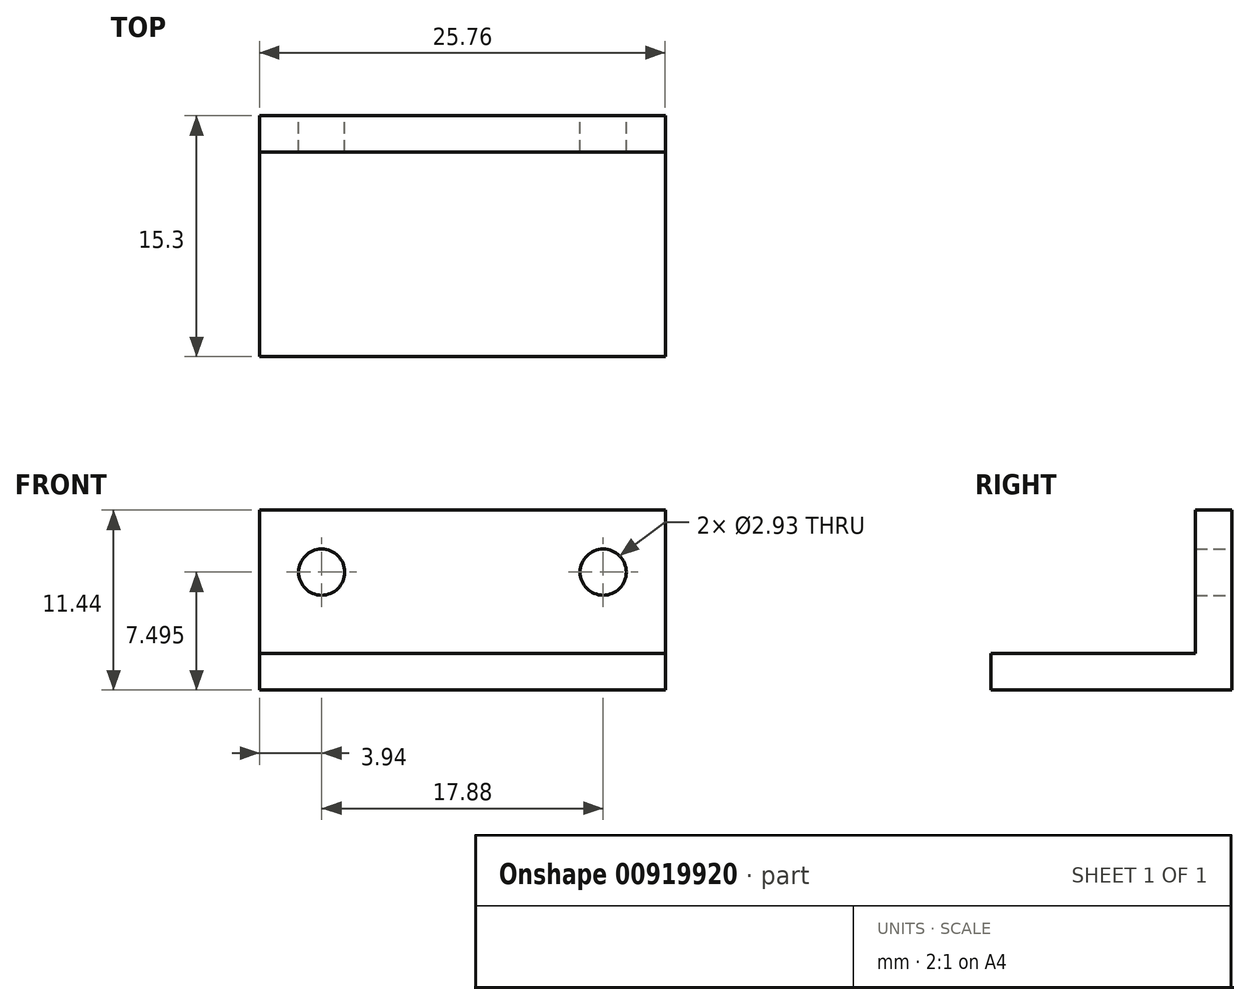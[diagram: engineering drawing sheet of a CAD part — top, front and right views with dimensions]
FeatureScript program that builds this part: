
annotation { "Feature Type Name" : "Feature", "Feature Type Description" : "" }
export const myFeature = defineFeature(function(context is Context, id is Id, definition is map)
    precondition{}
    {
        {
            var Q0;
            Q0=qCreatedBy(makeId("Front.planeOp"),FACE);
            var sketch = newSketch(context, id + "F0", { "sketchPlane" : qUnion([Q0])});
            skLineSegment(sketch, "E0.bottom", {"start": v(12.88, -5.72) * mm, "end": v(-12.88, -5.72) * mm});
            skLineSegment(sketch, "E0.top", {"start": v(12.88, 5.72) * mm, "end": v(-12.88, 5.72) * mm});
            skLineSegment(sketch, "E0.left", {"start": v(12.89, -5.72) * mm, "end": v(12.88, 5.72) * mm});
            skLineSegment(sketch, "E0.right", {"start": v(-12.88, -5.72) * mm, "end": v(-12.89, 5.72) * mm});
            skPoint(sketch, "E0.middle", {"position": v(0, 0) * mm});
            skCircle(sketch, "E1", {"center": v(-8.94, 1.78) * mm, "radius": 1.47 * mm});
            skCircle(sketch, "E2", {"center": v(8.94, 1.78) * mm, "radius": 1.47 * mm});
            skSolve(sketch);
        }
        {
            var Q0;
            Q0 = qSketchRegion(id + "F0", true);
            extrude(context, id + "F1", {"entities" : qUnion([Q0]), "depth" : 2.3 * mm, "offsetDistance" : 25 * mm});
        }
        {
            var Q0;
            Q0=makeQuery(id+"F1.opExtrude","CAP_FACE",FACE,{"disambiguationData":[OSD([sQuery(id+"F0.wireOp",EDGE,"E0.bottom"),sQuery(id+"F0.wireOp",EDGE,"E0.top"),sQuery(id+"F0.wireOp",EDGE,"E0.left"),sQuery(id+"F0.wireOp",EDGE,"E0.right"),sQuery(id+"F0.wireOp",EDGE,"E1"),sQuery(id+"F0.wireOp",EDGE,"E2")])],"isStart":false});
            var sketch = newSketch(context, id + "F2", { "sketchPlane" : qUnion([Q0])});
            skLineSegment(sketch, "E3.bottom", {"start": v(12.88, -5.72) * mm, "end": v(-12.88, -5.72) * mm});
            skLineSegment(sketch, "E3.top", {"start": v(12.88, -3.39) * mm, "end": v(-12.88, -3.39) * mm});
            skLineSegment(sketch, "E3.left", {"start": v(12.88, -5.72) * mm, "end": v(12.88, -3.39) * mm});
            skLineSegment(sketch, "E3.right", {"start": v(-12.88, -5.72) * mm, "end": v(-12.88, -3.39) * mm});
            skPoint(sketch, "E3.middle", {"position": v(0, -4.55) * mm});
            skSolve(sketch);
        }
        {
            var Q0;
            Q0 = qSketchRegion(id + "F2", true);
            extrude(context, id + "F3", {"entities" : qUnion([Q0]), "operationType" : NewBodyOperationType.ADD, "depth" : 13 * mm, "offsetDistance" : 25 * mm});
        }
    });
